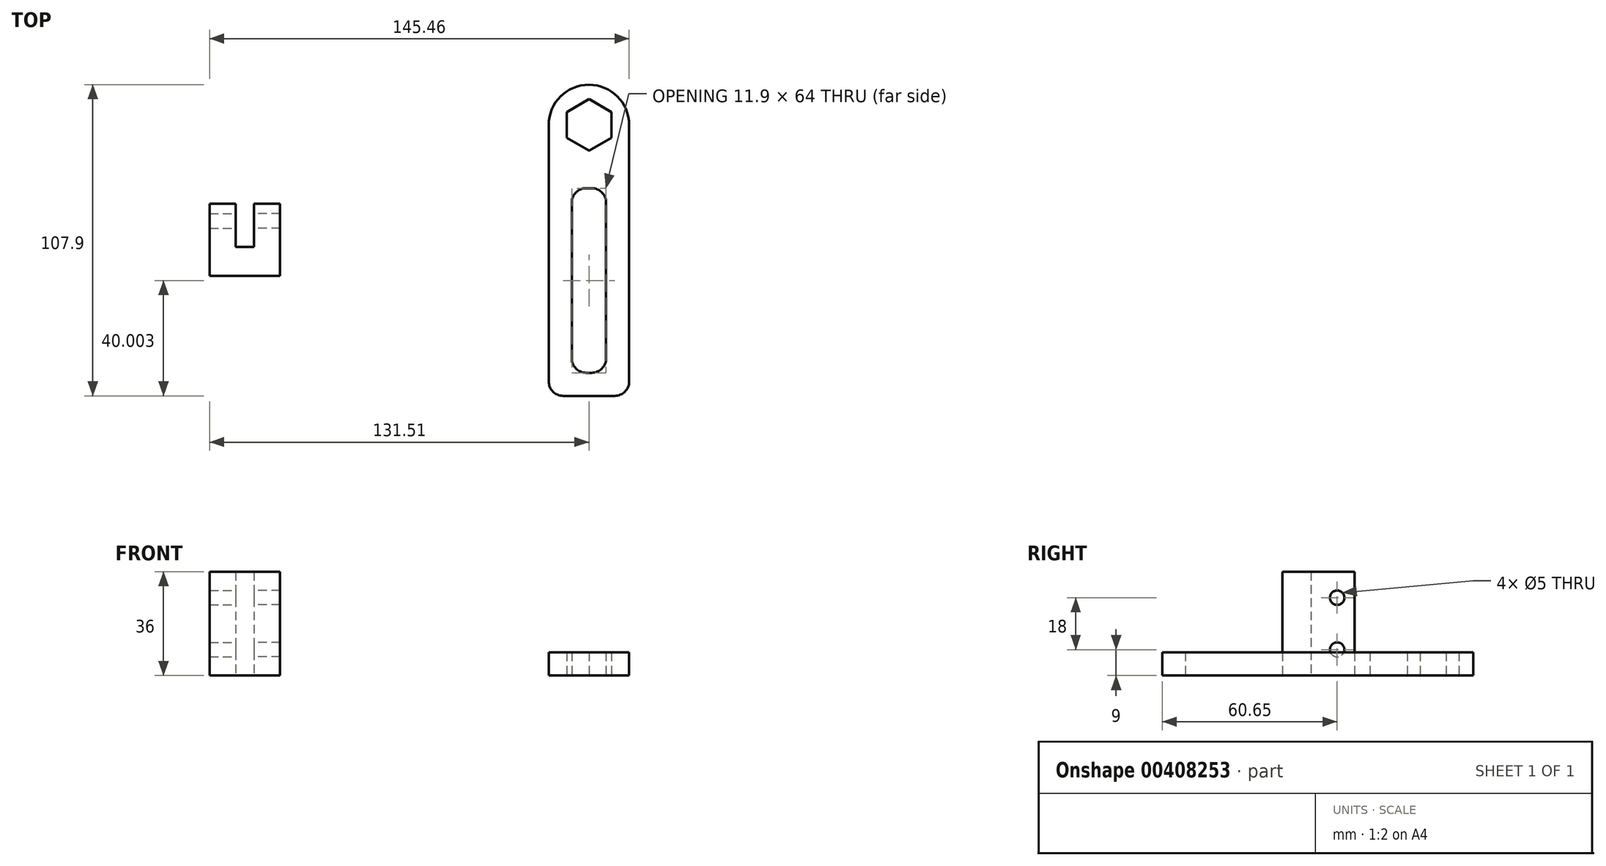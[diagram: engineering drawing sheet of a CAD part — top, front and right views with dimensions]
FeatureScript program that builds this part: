
annotation { "Feature Type Name" : "Feature", "Feature Type Description" : "" }
export const myFeature = defineFeature(function(context is Context, id is Id, definition is map)
    precondition{}
    {
        {
            var Q0;
            Q0=qCreatedBy(makeId("Top.planeOp"),FACE);
            var sketch = newSketch(context, id + "F0", { "sketchPlane" : qUnion([Q0])});
            skLineSegment(sketch, "E0", {"start": v(0, 0) * mm, "end": v(12.2, 0) * mm});
            skLineSegment(sketch, "E1", {"start": v(12.2, 0) * mm, "end": v(12.2, 25) * mm});
            skLineSegment(sketch, "E2", {"start": v(12.2, 25) * mm, "end": v(3.2, 25) * mm});
            skLineSegment(sketch, "E3", {"start": v(3.2, 25) * mm, "end": v(3.2, 10) * mm});
            skLineSegment(sketch, "E4", {"start": v(3.2, 10) * mm, "end": v(0, 10) * mm});
            skLineSegment(sketch, "E5", {"start": v(0, 10) * mm, "end": v(0, 0) * mm});
            skSolve(sketch);
        }
        {
            var Q0;
            Q0=makeQuery(id+"F0.imprint","IMPRINT",FACE,{"disambiguationData":[TD([[makeQuery(id+"F0.imprint","IMPRINT",EDGE,{"derivedFrom":sQuery(id+"F0.wireOp",EDGE,"E0")}),1.0]])]});
            extrude(context, id + "F1", {"entities" : qUnion([Q0]), "depth" : 36 * mm});
        }
        {
            var Q0;
            Q0=makeQuery(id+"F1.opExtrude","SWEPT_FACE",FACE,{"disambiguationData":[OSD([sQuery(id+"F0.wireOp",EDGE,"E3")])]});
            var sketch = newSketch(context, id + "F2", { "sketchPlane" : qUnion([Q0])});
            skCircle(sketch, "E6", {"center": v(-19, 27) * mm, "radius": 2.5 * mm});
            skCircle(sketch, "E7", {"center": v(-19, 9) * mm, "radius": 2.5 * mm});
            skCircle(sketch, "E8", {"center": v(-19, 27) * mm, "radius": 8 * mm, "construction": true});
            skCircle(sketch, "E9", {"center": v(-19, 9) * mm, "radius": 8 * mm, "construction": true});
            skSolve(sketch);
        }
        {
            var Q0;
            Q0=makeQuery(id+"F2.imprint","IMPRINT",FACE,{"disambiguationData":[TD([[makeQuery(id+"F2.imprint","IMPRINT",EDGE,{"derivedFrom":sQuery(id+"F2.wireOp",EDGE,"E6")}),1.0]])]});
            var Q1;
            Q1=makeQuery(id+"F2.imprint","IMPRINT",FACE,{"disambiguationData":[TD([[makeQuery(id+"F2.imprint","IMPRINT",EDGE,{"derivedFrom":sQuery(id+"F2.wireOp",EDGE,"E7")}),1.0]])]});
            extrude(context, id + "F3", {"entities" : qUnion([Q0, Q1]), "operationType" : NewBodyOperationType.REMOVE, "endBound" : BoundingType.THROUGH_ALL, "oppositeDirection" : true, "depth" : 25 * mm});
        }
        {
            var Q0;
            Q0=makeQuery(id+"F1.opExtrude","SWEPT_BODY",BODY,{"disambiguationData":[OSD([sQuery(id+"F0.wireOp",EDGE,"E0"),sQuery(id+"F0.wireOp",EDGE,"E1"),sQuery(id+"F0.wireOp",EDGE,"E2"),sQuery(id+"F0.wireOp",EDGE,"E3"),sQuery(id+"F0.wireOp",EDGE,"E4"),sQuery(id+"F0.wireOp",EDGE,"E5")])]});
            var Q1;
            Q1=makeQuery(id+"F1.opExtrude","SWEPT_FACE",FACE,{"disambiguationData":[OSD([sQuery(id+"F0.wireOp",EDGE,"E5")])]});
            mirror(context, id + "F4", {"operationType" : NewBodyOperationType.ADD, "entities" : qUnion([Q0]), "mirrorPlane" : qUnion([Q1])});
        }
        {
            var Q0;
            Q0=qCreatedBy(makeId("Top.planeOp"),FACE);
            var sketch = newSketch(context, id + "F5", { "sketchPlane" : qUnion([Q0])});
            skCircle(sketch, "E10.cCircle", {"center": v(119.31, 52.3) * mm, "radius": 7.75 * mm, "construction": true});
            skLineSegment(sketch, "E10.0", {"start": v(127.06, 47.83) * mm, "end": v(119.31, 43.35) * mm});
            skLineSegment(sketch, "E10.1", {"start": v(119.31, 43.35) * mm, "end": v(111.56, 47.83) * mm});
            skLineSegment(sketch, "E10.2", {"start": v(111.56, 47.83) * mm, "end": v(111.56, 56.78) * mm});
            skLineSegment(sketch, "E10.3", {"start": v(111.56, 56.78) * mm, "end": v(119.31, 61.25) * mm});
            skLineSegment(sketch, "E10.4", {"start": v(119.31, 61.25) * mm, "end": v(127.06, 56.78) * mm});
            skLineSegment(sketch, "E10.5", {"start": v(127.06, 56.78) * mm, "end": v(127.06, 47.83) * mm});
            skPoint(sketch, "E10.0.midPoint", {"position": v(123.19, 45.6) * mm});
            skCircle(sketch, "E11", {"center": v(119.31, 52.3) * mm, "radius": 13.95 * mm});
            skLineSegment(sketch, "E12", {"start": v(105.36, 52.3) * mm, "end": v(105.36, -36.65) * mm});
            skPoint(sketch, "E12.startSnap0", {"position": v(111.56, 52.3) * mm});
            skLineSegment(sketch, "E13", {"start": v(110.36, -41.65) * mm, "end": v(128.26, -41.65) * mm});
            skLineSegment(sketch, "E14", {"start": v(133.26, 52.3) * mm, "end": v(133.26, -36.65) * mm});
            skPoint(sketch, "E14.startSnap0", {"position": v(127.06, 52.3) * mm});
            skPoint(sketch, "E15.visualSharp", {"position": v(105.36, -41.65) * mm});
            skArc(sketch, "E15.filletArc", {"start": v(105.36, -36.65) * mm, "mid": v(106.83, -40.18) * mm, "end": v(110.36, -41.65) * mm});
            skPoint(sketch, "E16.visualSharp", {"position": v(133.26, -41.65) * mm});
            skArc(sketch, "E16.filletArc", {"start": v(128.26, -41.65) * mm, "mid": v(131.8, -40.18) * mm, "end": v(133.26, -36.65) * mm});
            skLineSegment(sketch, "E17.bottom", {"start": v(118.36, 30.35) * mm, "end": v(120.26, 30.35) * mm});
            skLineSegment(sketch, "E17.top", {"start": v(118.36, -33.65) * mm, "end": v(120.26, -33.65) * mm});
            skLineSegment(sketch, "E17.left", {"start": v(113.36, 25.35) * mm, "end": v(113.36, -28.65) * mm});
            skLineSegment(sketch, "E17.right", {"start": v(125.26, 25.35) * mm, "end": v(125.26, -28.65) * mm});
            skPoint(sketch, "E18.visualSharp", {"position": v(113.36, 30.35) * mm});
            skArc(sketch, "E18.filletArc", {"start": v(118.36, 30.35) * mm, "mid": v(114.83, 28.89) * mm, "end": v(113.36, 25.35) * mm});
            skPoint(sketch, "E19.visualSharp", {"position": v(125.26, 30.35) * mm});
            skArc(sketch, "E19.filletArc", {"start": v(125.26, 25.35) * mm, "mid": v(123.8, 28.89) * mm, "end": v(120.26, 30.35) * mm});
            skPoint(sketch, "E20.visualSharp", {"position": v(125.26, -33.65) * mm});
            skArc(sketch, "E20.filletArc", {"start": v(120.26, -33.65) * mm, "mid": v(123.8, -32.18) * mm, "end": v(125.26, -28.65) * mm});
            skPoint(sketch, "E21.visualSharp", {"position": v(113.36, -33.65) * mm});
            skArc(sketch, "E21.filletArc", {"start": v(113.36, -28.65) * mm, "mid": v(114.83, -32.18) * mm, "end": v(118.36, -33.65) * mm});
            skSolve(sketch);
        }
        {
            var Q0;
            {var subQ0=sQuery(id+"F5.wireOp",EDGE,"E12");Q0=makeQuery(id+"F5.imprint","IMPRINT",FACE,{"disambiguationData":[TD([[makeQuery(id+"F5.imprint","IMPRINT",EDGE,{"derivedFrom":subQ0}),1.0]])]});}
            var Q1;
            Q1=makeQuery(id+"F5.imprint","IMPRINT",FACE,{"disambiguationData":[TD([[makeQuery(id+"F5.imprint","IMPRINT",EDGE,{"derivedFrom":sQuery(id+"F5.wireOp",EDGE,"E10.0")}),1.0]])]});
            extrude(context, id + "F6", {"entities" : qUnion([Q0, Q1]), "depth" : 8 * mm, "offsetDistance" : 25 * mm});
        }
    });
